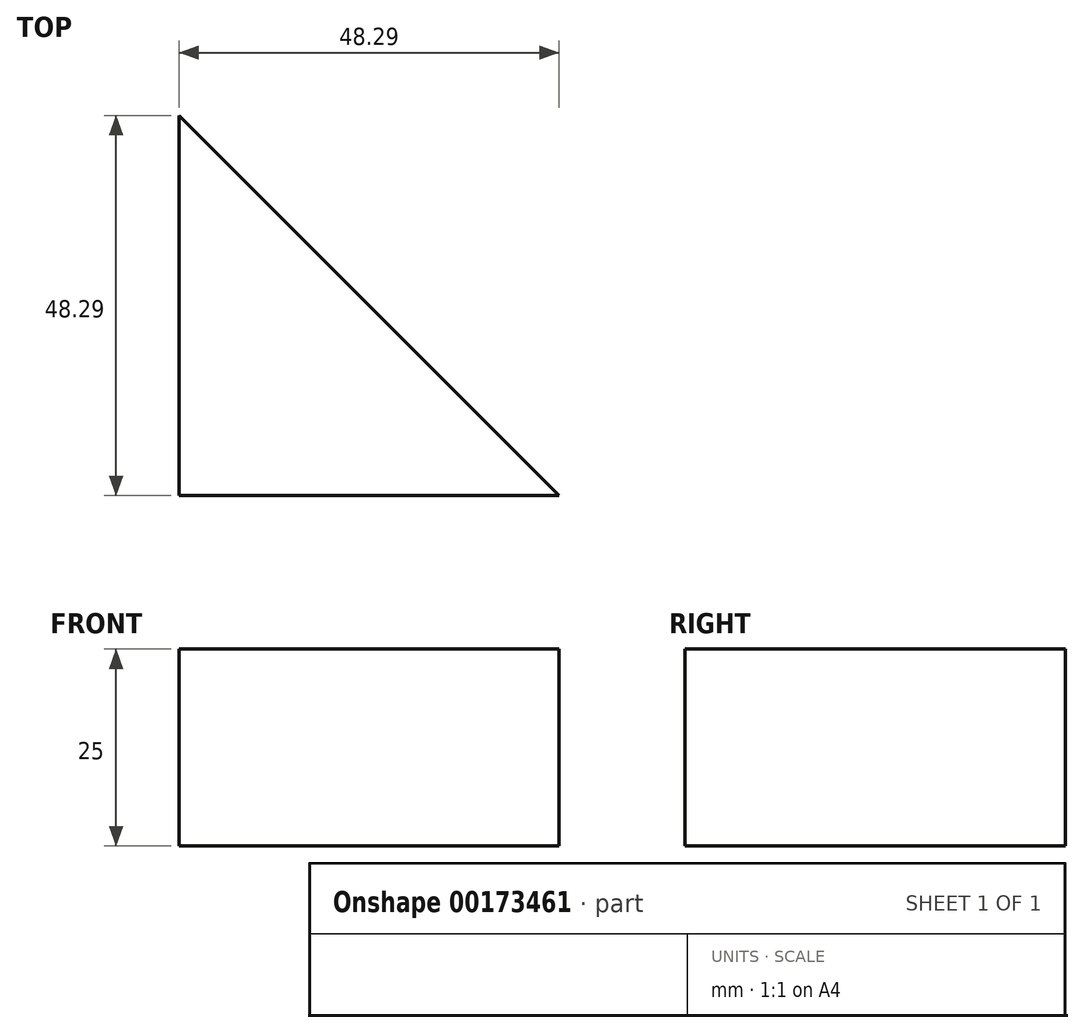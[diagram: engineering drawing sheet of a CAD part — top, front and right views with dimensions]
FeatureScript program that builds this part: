
annotation { "Feature Type Name" : "Feature", "Feature Type Description" : "" }
export const myFeature = defineFeature(function(context is Context, id is Id, definition is map)
    precondition{}
    {
        {
            var Q0;
            Q0=qCreatedBy(makeId("Top.planeOp"),FACE);
            var sketch = newSketch(context, id + "F0", { "sketchPlane" : qUnion([Q0])});
            skLineSegment(sketch, "E0", {"start": v(0, 0) * mm, "end": v(0, -48.29) * mm});
            skLineSegment(sketch, "E1", {"start": v(0, -48.29) * mm, "end": v(48.29, -48.29) * mm});
            skLineSegment(sketch, "E2", {"start": v(48.29, -48.29) * mm, "end": v(0, 0) * mm});
            skSolve(sketch);
        }
        {
            var Q0;
            Q0=makeQuery(id+"F0.imprint","IMPRINT",FACE,{"disambiguationData":[TD([[makeQuery(id+"F0.imprint","IMPRINT",EDGE,{"derivedFrom":sQuery(id+"F0.wireOp",EDGE,"E0")}),1.0]])]});
            extrude(context, id + "F1", {"entities" : qUnion([Q0]), "depth" : 25 * mm});
        }
    });
